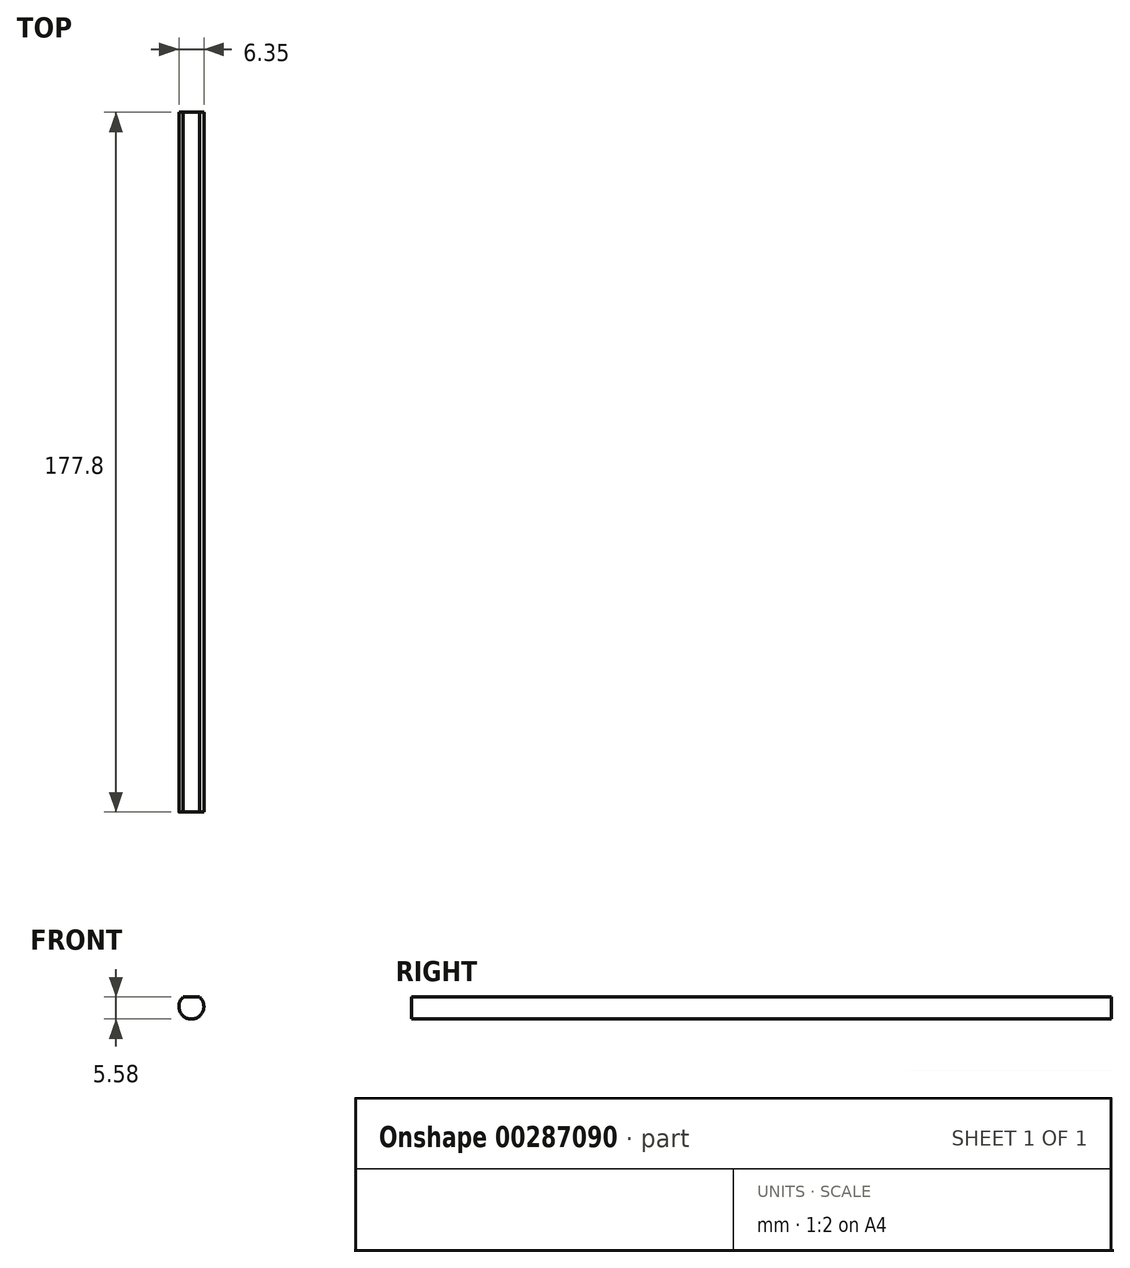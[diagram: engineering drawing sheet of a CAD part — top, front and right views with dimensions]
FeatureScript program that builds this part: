
annotation { "Feature Type Name" : "Feature", "Feature Type Description" : "" }
export const myFeature = defineFeature(function(context is Context, id is Id, definition is map)
    precondition{}
    {
        {
            var Q0;
            Q0=qCreatedBy(makeId("Front.planeOp"),FACE);
            var sketch = newSketch(context, id + "F0", { "sketchPlane" : qUnion([Q0])});
            skCircle(sketch, "E0", {"center": v(0, 0) * mm, "radius": 3.18 * mm});
            skLineSegment(sketch, "E1.bottom", {"start": v(-8.93, -4.24) * mm, "end": v(11.49, -4.24) * mm});
            skLineSegment(sketch, "E1.top", {"start": v(-8.93, 2.41) * mm, "end": v(11.49, 2.41) * mm});
            skLineSegment(sketch, "E1.left", {"start": v(-8.93, -4.24) * mm, "end": v(-8.93, 2.41) * mm});
            skLineSegment(sketch, "E1.right", {"start": v(11.49, -4.24) * mm, "end": v(11.49, 2.41) * mm});
            skSolve(sketch);
        }
        {
            var Q0;
            {var subQ0=sQuery(id+"F0.wireOp",EDGE,"E1.top");var subQ1=sQuery(id+"F0.wireOp",EDGE,"E0");var subQ2=makeQuery(id+"F0.imprint","INTERSECT",VERTEX,{"disambiguationData":[OD(0.0)],"derivedFrom":[subQ1,subQ0]});Q0=makeQuery(id+"F0.imprint","IMPRINT",FACE,{"disambiguationData":[TD([[makeQuery(id+"F0.imprint","IMPRINT",EDGE,{"disambiguationData":[TD([[subQ2,-1.0]])],"derivedFrom":subQ1}),1.0]])]});}
            extrude(context, id + "F1", {"entities" : qUnion([Q0]), "depth" : 177.8 * mm});
        }
    });
